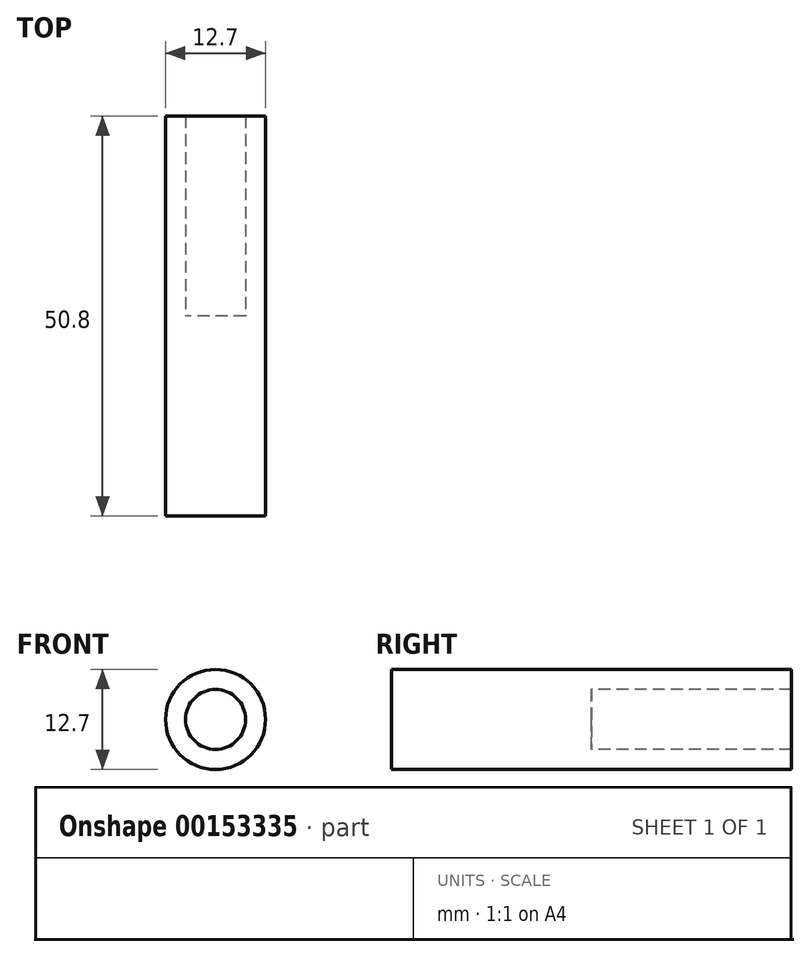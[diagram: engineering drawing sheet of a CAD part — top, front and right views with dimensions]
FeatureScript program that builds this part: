
annotation { "Feature Type Name" : "Feature", "Feature Type Description" : "" }
export const myFeature = defineFeature(function(context is Context, id is Id, definition is map)
    precondition{}
    {
        {
            var Q0;
            Q0=qCreatedBy(makeId("Front.planeOp"),FACE);
            var sketch = newSketch(context, id + "F0", { "sketchPlane" : qUnion([Q0])});
            skCircle(sketch, "E0", {"center": v(0, 0) * mm, "radius": 6.35 * mm});
            skSolve(sketch);
        }
        {
            var Q0;
            Q0=sQuery(id+"F0.wireOp",EDGE,"E0");
            extrude(context, id + "F1", {"bodyType" : ToolBodyType.SURFACE, "surfaceEntities" : qUnion([Q0]), "depth" : 50.8 * mm});
        }
        {
            var Q0;
            Q0=qCreatedBy(makeId("Front.planeOp"),FACE);
            var sketch = newSketch(context, id + "F2", { "sketchPlane" : qUnion([Q0])});
            skLineSegment(sketch, "E1.bottom", {"start": v(3.81, -3.8) * mm, "end": v(-3.81, -3.81) * mm});
            skLineSegment(sketch, "E1.top", {"start": v(3.81, 3.81) * mm, "end": v(-3.81, 3.81) * mm});
            skLineSegment(sketch, "E1.left", {"start": v(3.8, -3.81) * mm, "end": v(3.81, 3.81) * mm});
            skLineSegment(sketch, "E1.right", {"start": v(-3.81, -3.81) * mm, "end": v(-3.8, 3.8) * mm});
            skPoint(sketch, "E1.middle", {"position": v(0, 0) * mm});
            skCircle(sketch, "E2", {"center": v(0, 0) * mm, "radius": 3.81 * mm});
            skSolve(sketch);
        }
        {
            var Q0;
            Q0=sQuery(id+"F2.wireOp",EDGE,"E2");
            extrude(context, id + "F3", {"bodyType" : ToolBodyType.SURFACE, "surfaceEntities" : qUnion([Q0]), "depth" : 25.4 * mm});
        }
    });
